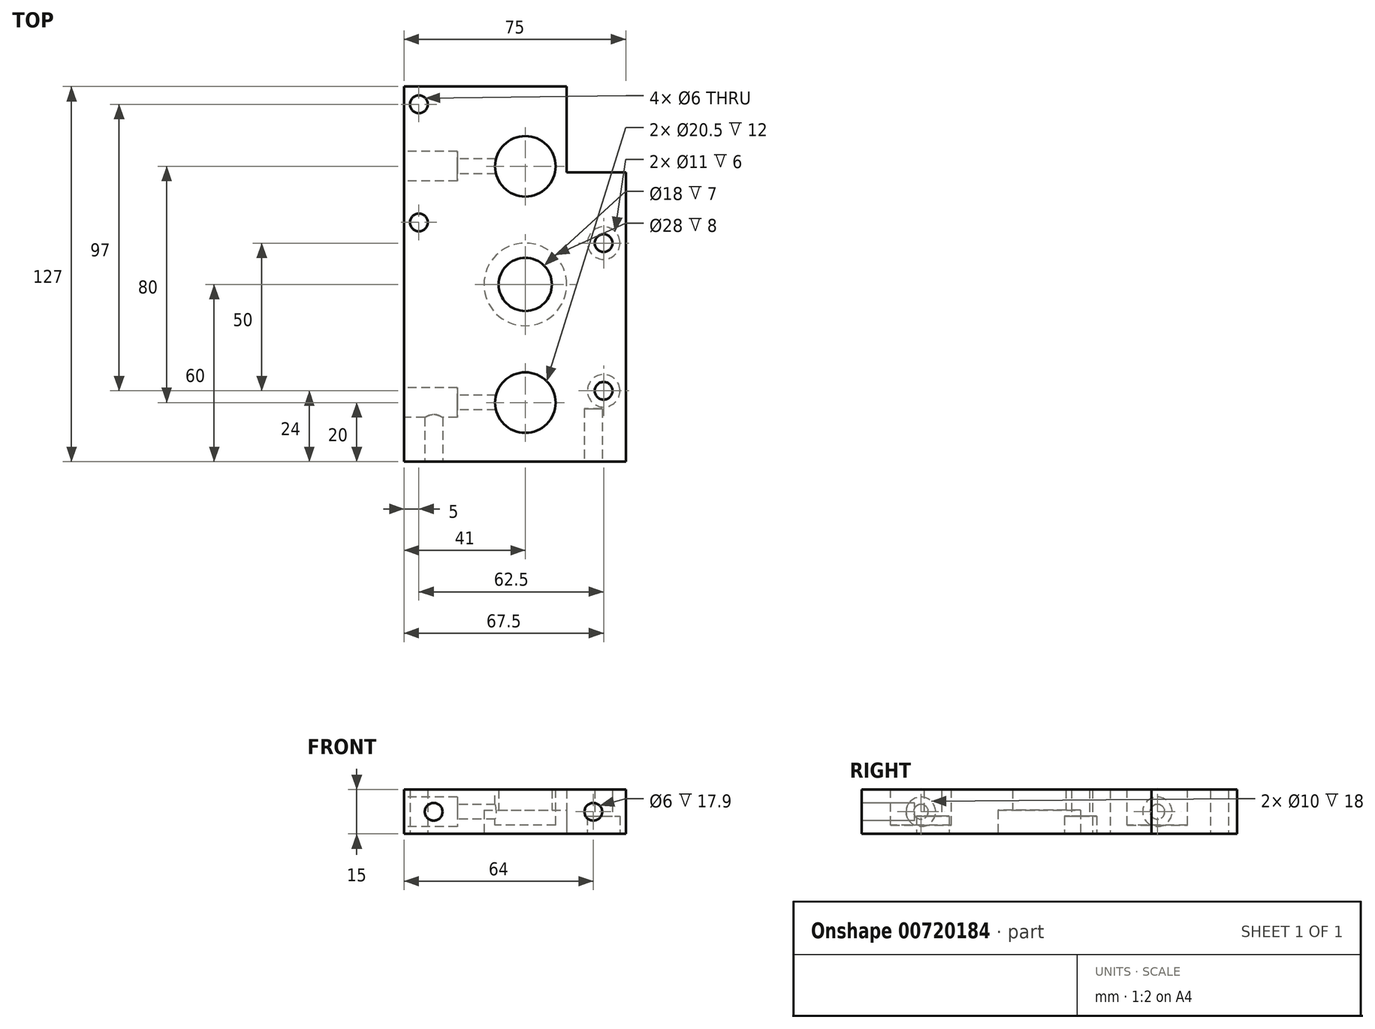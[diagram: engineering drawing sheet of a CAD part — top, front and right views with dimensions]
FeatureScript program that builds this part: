
annotation { "Feature Type Name" : "Feature", "Feature Type Description" : "" }
export const myFeature = defineFeature(function(context is Context, id is Id, definition is map)
    precondition{}
    {
        {
            var Q0;
            Q0=qCreatedBy(makeId("Top.planeOp"),FACE);
            var sketch = newSketch(context, id + "F0", { "sketchPlane" : qUnion([Q0])});
            skLineSegment(sketch, "E0.bottom", {"start": v(0, 0) * mm, "end": v(75, 0) * mm});
            skLineSegment(sketch, "E0.top", {"start": v(0, 127) * mm, "end": v(55, 127) * mm});
            skLineSegment(sketch, "E0.left", {"start": v(0, 0) * mm, "end": v(0, 127) * mm});
            skLineSegment(sketch, "E1.0", {"start": v(55, 98) * mm, "end": v(75, 98) * mm});
            skLineSegment(sketch, "E2.0", {"start": v(55, 98) * mm, "end": v(55, 127) * mm});
            skLineSegment(sketch, "E3", {"start": v(75, 0) * mm, "end": v(75, 0) * mm});
            skLineSegment(sketch, "E4", {"start": v(75, 0) * mm, "end": v(75, 98) * mm});
            skLineSegment(sketch, "E5", {"start": v(75, 98) * mm, "end": v(75, 98) * mm});
            skSolve(sketch);
        }
        {
            var Q0;
            Q0 = qSketchRegion(id + "F0", true);
            extrude(context, id + "F1", {"entities" : qUnion([Q0]), "depth" : 15 * mm, "offsetDistance" : 25 * mm});
        }
        {
            var Q0;
            Q0=makeQuery(id+"F1.opExtrude","CAP_FACE",FACE,{"disambiguationData":[OSD([sQuery(id+"F0.wireOp",EDGE,"E0.bottom"),sQuery(id+"F0.wireOp",EDGE,"E0.top"),sQuery(id+"F0.wireOp",EDGE,"E0.left"),sQuery(id+"F0.wireOp",EDGE,"E0.right"),sQuery(id+"F0.wireOp",EDGE,"E1.0"),sQuery(id+"F0.wireOp",EDGE,"E2.0")])],"isStart":true});
            var sketch = newSketch(context, id + "F2", { "sketchPlane" : qUnion([Q0])});
            skCircle(sketch, "E6", {"center": v(5, -121) * mm, "radius": 3 * mm});
            skCircle(sketch, "E7", {"center": v(5, -81) * mm, "radius": 3 * mm});
            skCircle(sketch, "E8", {"center": v(41, -60) * mm, "radius": 9 * mm});
            skCircle(sketch, "E9", {"center": v(67.5, -24) * mm, "radius": 3 * mm});
            skCircle(sketch, "E10", {"center": v(67.5, -74) * mm, "radius": 3 * mm});
            skSolve(sketch);
        }
        {
            var Q0;
            Q0 = qSketchRegion(id + "F2", true);
            extrude(context, id + "F3", {"entities" : qUnion([Q0]), "operationType" : NewBodyOperationType.REMOVE, "endBound" : BoundingType.THROUGH_ALL, "oppositeDirection" : true, "depth" : 25 * mm, "offsetDistance" : 25 * mm});
        }
        {
            var Q0;
            Q0=makeQuery(id+"F1.opExtrude","CAP_FACE",FACE,{"disambiguationData":[OSD([sQuery(id+"F0.wireOp",EDGE,"E0.bottom"),sQuery(id+"F0.wireOp",EDGE,"E0.top"),sQuery(id+"F0.wireOp",EDGE,"E0.left"),sQuery(id+"F0.wireOp",EDGE,"E0.right"),sQuery(id+"F0.wireOp",EDGE,"E1.0"),sQuery(id+"F0.wireOp",EDGE,"E2.0")])],"isStart":true});
            var sketch = newSketch(context, id + "F4", { "sketchPlane" : qUnion([Q0])});
            skCircle(sketch, "E11", {"center": v(67.5, -74) * mm, "radius": 5.5 * mm});
            skCircle(sketch, "E12", {"center": v(67.5, -24) * mm, "radius": 5.5 * mm});
            skSolve(sketch);
        }
        {
            var Q0;
            Q0=makeQuery(id+"F4.imprint","IMPRINT",FACE,{"disambiguationData":[TD([[makeQuery(id+"F4.imprint","IMPRINT",EDGE,{"derivedFrom":sQuery(id+"F4.wireOp",EDGE,"E11")}),1.0]])]});
            var Q1;
            Q1=makeQuery(id+"F4.imprint","IMPRINT",FACE,{"disambiguationData":[TD([[makeQuery(id+"F4.imprint","IMPRINT",EDGE,{"derivedFrom":sQuery(id+"F4.wireOp",EDGE,"E12")}),1.0]])]});
            extrude(context, id + "F5", {"entities" : qUnion([Q0, Q1]), "operationType" : NewBodyOperationType.REMOVE, "oppositeDirection" : true, "depth" : 6 * mm, "offsetDistance" : 25 * mm});
        }
        {
            var Q0;
            Q0=makeQuery(id+"F1.opExtrude","CAP_FACE",FACE,{"disambiguationData":[OSD([sQuery(id+"F0.wireOp",EDGE,"E0.bottom"),sQuery(id+"F0.wireOp",EDGE,"E0.top"),sQuery(id+"F0.wireOp",EDGE,"E0.left"),sQuery(id+"F0.wireOp",EDGE,"E0.right"),sQuery(id+"F0.wireOp",EDGE,"E1.0"),sQuery(id+"F0.wireOp",EDGE,"E2.0")])],"isStart":false});
            var sketch = newSketch(context, id + "F6", { "sketchPlane" : qUnion([Q0])});
            skCircle(sketch, "E13", {"center": v(41, 20) * mm, "radius": 10.25 * mm});
            skCircle(sketch, "E14", {"center": v(41, 100) * mm, "radius": 10.25 * mm});
            skSolve(sketch);
        }
        {
            var Q0;
            Q0=makeQuery(id+"F6.imprint","IMPRINT",FACE,{"disambiguationData":[TD([[makeQuery(id+"F6.imprint","IMPRINT",EDGE,{"derivedFrom":sQuery(id+"F6.wireOp",EDGE,"E14")}),1.0]])]});
            var Q1;
            Q1=makeQuery(id+"F6.imprint","IMPRINT",FACE,{"disambiguationData":[TD([[makeQuery(id+"F6.imprint","IMPRINT",EDGE,{"derivedFrom":sQuery(id+"F6.wireOp",EDGE,"E13")}),1.0]])]});
            extrude(context, id + "F7", {"entities" : qUnion([Q0, Q1]), "operationType" : NewBodyOperationType.REMOVE, "oppositeDirection" : true, "depth" : 12 * mm, "offsetDistance" : 25 * mm});
        }
        {
            var Q0;
            Q0=makeQuery(id+"F1.opExtrude","SWEPT_FACE",FACE,{"disambiguationData":[OSD([sQuery(id+"F0.wireOp",EDGE,"E0.left")])]});
            var sketch = newSketch(context, id + "F8", { "sketchPlane" : qUnion([Q0])});
            skCircle(sketch, "E15", {"center": v(-100, 7.5) * mm, "radius": 2.5 * mm});
            skPoint(sketch, "E15.centerSnap0", {"position": v(-127, 7.5) * mm});
            skCircle(sketch, "E16", {"center": v(-20, 7.5) * mm, "radius": 2.5 * mm});
            skSolve(sketch);
        }
        {
            var Q0;
            Q0=sQuery(id+"F8.wireOp",VERTEX,"E15.center");
            var Q1;
            Q1=sQuery(id+"F8.wireOp",VERTEX,"E16.center");
            var Q2;
            Q2=makeQuery(id+"F1.opExtrude","SWEPT_BODY",BODY,{"disambiguationData":[OSD([sQuery(id+"F0.wireOp",EDGE,"E0.bottom"),sQuery(id+"F0.wireOp",EDGE,"E0.top"),sQuery(id+"F0.wireOp",EDGE,"E0.left"),sQuery(id+"F0.wireOp",EDGE,"E0.right"),sQuery(id+"F0.wireOp",EDGE,"E1.0"),sQuery(id+"F0.wireOp",EDGE,"E2.0")])]});
            hole(context, id + "F9", {"style" : HoleStyle.SIMPLE, "endStyle" : HoleEndStyle.BLIND, "holeDiameter" : 5 * mm, "majorDiameter" : 5 * mm, "holeDepth" : 35 * mm, "isTappedThrough" : true, "tappedDepth" : 12 * mm, "tapClearance" : 3, "startFromSketch" : true, "locations" : qUnion([Q0, Q1]), "scope" : qUnion([Q2])});
        }
        {
            var Q0;
            Q0=makeQuery(id+"F1.opExtrude","SWEPT_FACE",FACE,{"disambiguationData":[OSD([sQuery(id+"F0.wireOp",EDGE,"E0.left")])]});
            var sketch = newSketch(context, id + "F10", { "sketchPlane" : qUnion([Q0])});
            skCircle(sketch, "E17", {"center": v(-100, 7.5) * mm, "radius": 5 * mm});
            skCircle(sketch, "E18", {"center": v(-20, 7.5) * mm, "radius": 5 * mm});
            skSolve(sketch);
        }
        {
            var Q0;
            Q0=makeQuery(id+"F10.imprint","IMPRINT",FACE,{"disambiguationData":[TD([[makeQuery(id+"F10.imprint","IMPRINT",EDGE,{"derivedFrom":sQuery(id+"F10.wireOp",EDGE,"E17")}),1.0]])]});
            var Q1;
            Q1=makeQuery(id+"F10.imprint","IMPRINT",FACE,{"disambiguationData":[TD([[makeQuery(id+"F10.imprint","IMPRINT",EDGE,{"derivedFrom":sQuery(id+"F10.wireOp",EDGE,"E18")}),1.0]])]});
            extrude(context, id + "F11", {"entities" : qUnion([Q0, Q1]), "operationType" : NewBodyOperationType.REMOVE, "oppositeDirection" : true, "depth" : 18 * mm, "offsetDistance" : 25 * mm});
        }
        {
            var Q0;
            Q0=makeQuery(id+"F1.opExtrude","SWEPT_FACE",FACE,{"disambiguationData":[OSD([sQuery(id+"F0.wireOp",EDGE,"E0.bottom")])]});
            var sketch = newSketch(context, id + "F12", { "sketchPlane" : qUnion([Q0])});
            skCircle(sketch, "E19", {"center": v(10, 7.5) * mm, "radius": 3 * mm});
            skPoint(sketch, "E19.centerSnap0", {"position": v(0, 7.5) * mm});
            skCircle(sketch, "E20", {"center": v(64, 7.5) * mm, "radius": 3 * mm});
            skSolve(sketch);
        }
        {
            var Q0;
            Q0=makeQuery(id+"F12.imprint","IMPRINT",FACE,{"disambiguationData":[TD([[makeQuery(id+"F12.imprint","IMPRINT",EDGE,{"derivedFrom":sQuery(id+"F12.wireOp",EDGE,"E19")}),1.0]])]});
            var Q1;
            Q1=makeQuery(id+"F12.imprint","IMPRINT",FACE,{"disambiguationData":[TD([[makeQuery(id+"F12.imprint","IMPRINT",EDGE,{"derivedFrom":sQuery(id+"F12.wireOp",EDGE,"E20")}),1.0]])]});
            extrude(context, id + "F13", {"entities" : qUnion([Q0, Q1]), "operationType" : NewBodyOperationType.REMOVE, "oppositeDirection" : true, "depth" : 17.9 * mm, "offsetDistance" : 25 * mm});
        }
        {
            var Q0;
            Q0=makeQuery(id+"F1.opExtrude","CAP_FACE",FACE,{"disambiguationData":[OSD([sQuery(id+"F0.wireOp",EDGE,"E0.bottom"),sQuery(id+"F0.wireOp",EDGE,"E0.top"),sQuery(id+"F0.wireOp",EDGE,"E0.left"),sQuery(id+"F0.wireOp",EDGE,"E1.0"),sQuery(id+"F0.wireOp",EDGE,"E2.0"),sQuery(id+"F0.wireOp",EDGE,"E4")])],"isStart":true});
            var sketch = newSketch(context, id + "F14", { "sketchPlane" : qUnion([Q0])});
            skCircle(sketch, "E21", {"center": v(41, -60) * mm, "radius": 14 * mm});
            skSolve(sketch);
        }
        {
            var Q0;
            Q0=makeQuery(id+"F14.imprint","IMPRINT",FACE,{"disambiguationData":[TD([[makeQuery(id+"F14.imprint","IMPRINT",EDGE,{"derivedFrom":sQuery(id+"F14.wireOp",EDGE,"E21")}),1.0]])]});
            extrude(context, id + "F15", {"entities" : qUnion([Q0]), "operationType" : NewBodyOperationType.REMOVE, "oppositeDirection" : true, "depth" : 8 * mm, "offsetDistance" : 25 * mm});
        }
    });
